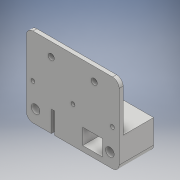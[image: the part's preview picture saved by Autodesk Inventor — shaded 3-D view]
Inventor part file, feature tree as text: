
AUTODESK INVENTOR PART (.ipt)
format: ipt  version: 2017 (Build 210142000, 142)  size: 349,184 bytes
history: native  units: mm
features: sketch x11, extrude x8, fillet x7, hole x4
ambient origin geometry x8: Origin, YZ Plane, XZ Plane, XY Plane, X Axis, Y Axis, Z Axis, Center Point
bodies: Solide1 (feature_tree)
feature tree (30):
  extrude  "Extrusion1"  Depth=40.0mm
  hole  "Perçage1"  [1 undecoded]
  extrude  "Extrusion2"  Depth=3.0mm TaperAngle=0.0deg
  extrude  "Extrusion3"  Depth=10.0mm
  hole  "Perçage2"  [1 undecoded]
  extrude  "Extrusion4"  Depth=16.22mm
  fillet  "Congé1"  Radius=3.0mm
  fillet  "Congé2"  Radius=40.0mm
  fillet  "Congé3"  Radius=3.0mm
  fillet  "Congé4"  Radius=37.0mm
  fillet  "Congé5"  Radius=10.0mm
  sketch  "Esquisse8"
  extrude  "Extrusion9"  Depth=16.22mm
  fillet  "Congé9"  Radius=10.0mm
  fillet  "Congé10"  Radius=5.0mm
  extrude  "Extrusion10"  Depth=5.0mm
  extrude  "Extrusion11"  Depth=5.0mm
  hole  "Perçage3"  [1 undecoded]
  extrude  "Extrusion12"  Depth=5.0mm
  hole  "Perçage4"  [1 undecoded]
  sketch  "Esquisse1"
  sketch  "Esquisse2"
  sketch  "Esquisse3"
  sketch  "Esquisse4"
  sketch  "Esquisse5"
  sketch  "Esquisse10"
  sketch  "Esquisse11"
  sketch  "Esquisse12"
  sketch  "Esquisse13"
  sketch  "Esquisse14"
note: 4 required parameter values undecoded (feature->parameter linkage not recoverable at this tier; creation-order binding heuristic only, values carry confidence <= 0.55)
